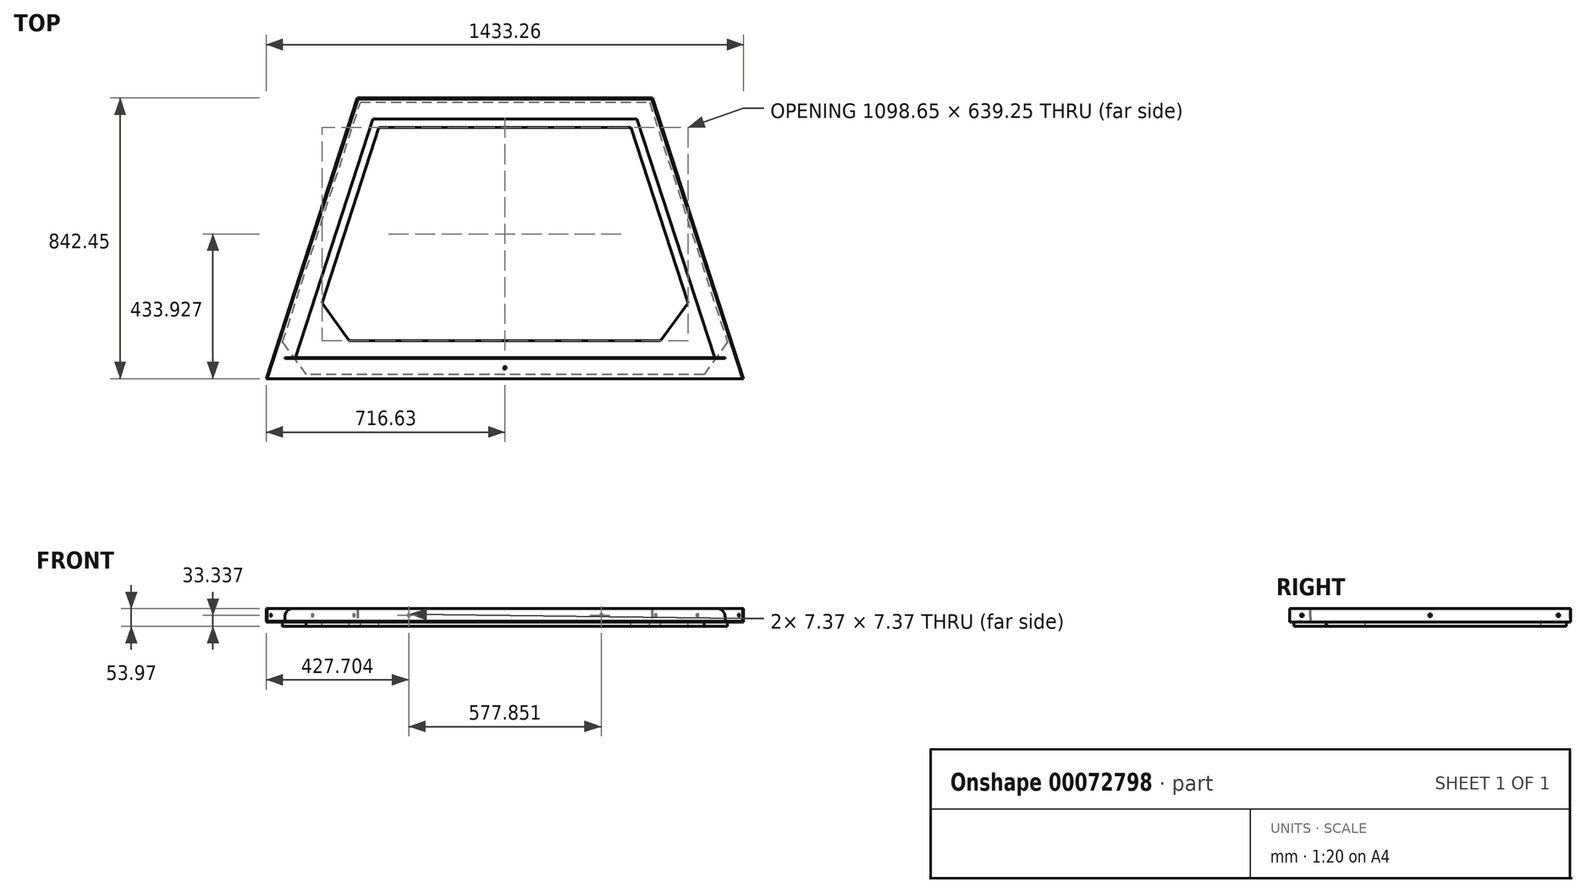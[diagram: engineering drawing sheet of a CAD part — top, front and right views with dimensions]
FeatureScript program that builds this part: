
annotation { "Feature Type Name" : "Feature", "Feature Type Description" : "" }
export const myFeature = defineFeature(function(context is Context, id is Id, definition is map)
    precondition{}
    {
        {
            var Q0;
            Q0=qCreatedBy(makeId("Top.planeOp"),FACE);
            var sketch = newSketch(context, id + "F0", { "sketchPlane" : qUnion([Q0])});
            skCircle(sketch, "E0.cCircle", {"center": v(0, 0) * mm, "radius": 609.6 * mm, "construction": true});
            skLineSegment(sketch, "E0.0", {"start": v(-716.63, -232.85) * mm, "end": v(-442.9, 609.6) * mm});
            skLineSegment(sketch, "E0.1", {"start": v(-442.9, 609.6) * mm, "end": v(442.9, 609.6) * mm});
            skLineSegment(sketch, "E0.2", {"start": v(442.9, 609.6) * mm, "end": v(716.63, -232.85) * mm});
            skPoint(sketch, "E0.0.midPoint", {"position": v(-579.76, 188.38) * mm});
            skLineSegment(sketch, "E1", {"start": v(-716.63, -232.85) * mm, "end": v(716.63, -232.85) * mm});
            skPoint(sketch, "E2.orphan", {"position": v(0, -753.5) * mm});
            skLineSegment(sketch, "E3.0", {"start": v(-629.23, -169.35) * mm, "end": v(-396.76, 546.1) * mm});
            skLineSegment(sketch, "E3.1", {"start": v(-629.23, -169.35) * mm, "end": v(629.23, -169.35) * mm});
            skLineSegment(sketch, "E3.2", {"start": v(396.76, 546.1) * mm, "end": v(629.23, -169.35) * mm});
            skLineSegment(sketch, "E3.3", {"start": v(-396.76, 546.1) * mm, "end": v(396.76, 546.1) * mm});
            skLineSegment(sketch, "E4.0", {"start": v(440.6, 606.43) * mm, "end": v(713.29, -232.85) * mm});
            skLineSegment(sketch, "E4.1", {"start": v(-440.6, 606.43) * mm, "end": v(440.6, 606.43) * mm});
            skLineSegment(sketch, "E4.2", {"start": v(-713.29, -232.85) * mm, "end": v(-440.6, 606.43) * mm});
            skSolve(sketch);
        }
        {
            var Q0;
            Q0=makeQuery(id+"F0.imprint","IMPRINT",FACE,{"disambiguationData":[TD([[makeQuery(id+"F0.imprint","IMPRINT",EDGE,{"derivedFrom":sQuery(id+"F0.wireOp",EDGE,"E0.0")}),-1.0]])]});
            var Q1;
            Q1=makeQuery(id+"F0.imprint","IMPRINT",FACE,{"disambiguationData":[TD([[makeQuery(id+"F0.imprint","IMPRINT",EDGE,{"derivedFrom":sQuery(id+"F0.wireOp",EDGE,"E3.0")}),1.0]])]});
            extrude(context, id + "F1", {"entities" : qUnion([Q0, Q1]), "depth" : 3.17 * mm});
        }
        {
            var Q0;
            Q0=makeQuery(id+"F1.opExtrude","CAP_FACE",FACE,{"disambiguationData":[OSD([sQuery(id+"F0.wireOp",EDGE,"E0.0"),sQuery(id+"F0.wireOp",EDGE,"E0.1"),sQuery(id+"F0.wireOp",EDGE,"E0.2"),sQuery(id+"F0.wireOp",EDGE,"E1"),sQuery(id+"F0.wireOp",EDGE,"E3.0"),sQuery(id+"F0.wireOp",EDGE,"E3.1"),sQuery(id+"F0.wireOp",EDGE,"E3.2"),sQuery(id+"F0.wireOp",EDGE,"E3.3")])],"isStart":false});
            var sketch = newSketch(context, id + "F2", { "sketchPlane" : qUnion([Q0])});
            skLineSegment(sketch, "E5.0", {"start": v(-716.63, -232.85) * mm, "end": v(-442.9, 609.6) * mm});
            skLineSegment(sketch, "E6.0", {"start": v(-442.9, 609.6) * mm, "end": v(442.9, 609.6) * mm});
            skLineSegment(sketch, "E7.0", {"start": v(442.9, 609.6) * mm, "end": v(716.63, -232.85) * mm});
            skLineSegment(sketch, "E8.0", {"start": v(440.6, 606.42) * mm, "end": v(713.29, -232.85) * mm});
            skLineSegment(sketch, "E9.0", {"start": v(-440.6, 606.43) * mm, "end": v(440.6, 606.43) * mm});
            skLineSegment(sketch, "E10.0", {"start": v(-713.29, -232.85) * mm, "end": v(-440.6, 606.43) * mm});
            skLineSegment(sketch, "E11", {"start": v(-716.63, -232.85) * mm, "end": v(-713.29, -232.85) * mm});
            skLineSegment(sketch, "E12", {"start": v(716.63, -232.85) * mm, "end": v(713.29, -232.85) * mm});
            skSolve(sketch);
        }
        {
            var Q0;
            Q0=makeQuery(id+"F2.imprint","IMPRINT",FACE,{"disambiguationData":[TD([[makeQuery(id+"F2.imprint","IMPRINT",EDGE,{"derivedFrom":sQuery(id+"F2.wireOp",EDGE,"E5.0")}),-1.0]])]});
            extrude(context, id + "F3", {"entities" : qUnion([Q0]), "operationType" : NewBodyOperationType.ADD, "depth" : 38.1 * mm});
        }
        {
            var Q0;
            Q0=makeQuery(id+"F1.opExtrude","CAP_FACE",FACE,{"disambiguationData":[OSD([sQuery(id+"F0.wireOp",EDGE,"E0.0"),sQuery(id+"F0.wireOp",EDGE,"E0.1"),sQuery(id+"F0.wireOp",EDGE,"E0.2"),sQuery(id+"F0.wireOp",EDGE,"E1"),sQuery(id+"F0.wireOp",EDGE,"E3.0"),sQuery(id+"F0.wireOp",EDGE,"E3.1"),sQuery(id+"F0.wireOp",EDGE,"E3.2"),sQuery(id+"F0.wireOp",EDGE,"E3.3")])],"isStart":false});
            var sketch = newSketch(context, id + "F4", { "sketchPlane" : qUnion([Q0])});
            skLineSegment(sketch, "E13.0", {"start": v(-629.23, -169.35) * mm, "end": v(629.23, -169.35) * mm});
            skLineSegment(sketch, "E14.0", {"start": v(-660.98, -172.43) * mm, "end": v(660.98, -172.43) * mm});
            skLineSegment(sketch, "E15", {"start": v(-629.23, -169.35) * mm, "end": v(-660.98, -169.35) * mm});
            skLineSegment(sketch, "E16", {"start": v(-660.98, -169.35) * mm, "end": v(-660.98, -172.43) * mm});
            skLineSegment(sketch, "E17", {"start": v(629.23, -169.35) * mm, "end": v(660.98, -169.35) * mm});
            skLineSegment(sketch, "E18", {"start": v(660.98, -169.35) * mm, "end": v(660.98, -172.43) * mm});
            skSolve(sketch);
        }
        {
            var Q0;
            Q0=makeQuery(id+"F4.imprint","IMPRINT",FACE,{"disambiguationData":[TD([[makeQuery(id+"F4.imprint","IMPRINT",EDGE,{"derivedFrom":sQuery(id+"F4.wireOp",EDGE,"E13.0")}),-1.0]])]});
            extrude(context, id + "F5", {"entities" : qUnion([Q0]), "operationType" : NewBodyOperationType.ADD, "depth" : 38.1 * mm});
        }
        {
            var Q0;
            Q0=makeQuery(id+"F5.opExtrude","CAP_EDGE",EDGE,{"disambiguationData":[OSD([sQuery(id+"F4.wireOp",EDGE,"E18")])],"isStart":false});
            var Q1;
            Q1=makeQuery(id+"F5.opExtrude","CAP_EDGE",EDGE,{"disambiguationData":[OSD([sQuery(id+"F4.wireOp",EDGE,"E16")])],"isStart":false});
            fillet(context, id + "F6", {"entities" : qUnion([Q0, Q1]), "radius" : 25.4 * mm, "tangentPropagation" : true, "allowEdgeOverflow" : false});
        }
        {
            var Q0;
            Q0=makeQuery(id+"F3.boolean.opBoolean","MERGE",FACE,{"derivedFrom":[makeQuery(id+"F1.opExtrude","SWEPT_FACE",FACE,{"disambiguationData":[OSD([sQuery(id+"F0.wireOp",EDGE,"E0.2")])]}),makeQuery(id+"F3.opExtrude","SWEPT_FACE",FACE,{"disambiguationData":[OSD([sQuery(id+"F2.wireOp",EDGE,"E7.0")])]})]});
            var sketch = newSketch(context, id + "F7", { "sketchPlane" : qUnion([Q0])});
            skLineSegment(sketch, "E19", {"start": v(442.9, 20.64) * mm, "end": v(404.8, 20.64) * mm, "construction": true});
            skLineSegment(sketch, "E20.rect.bottom", {"start": v(401.12, 16.95) * mm, "end": v(408.48, 16.95) * mm});
            skLineSegment(sketch, "E20.rect.top", {"start": v(401.12, 24.32) * mm, "end": v(408.48, 24.32) * mm});
            skLineSegment(sketch, "E20.rect.left", {"start": v(401.12, 16.95) * mm, "end": v(401.12, 24.32) * mm});
            skLineSegment(sketch, "E20.rect.right", {"start": v(408.48, 16.95) * mm, "end": v(408.48, 24.32) * mm});
            skPoint(sketch, "E20.rect.middle", {"position": v(404.8, 20.64) * mm});
            skLineSegment(sketch, "E21", {"start": v(404.8, 20.64) * mm, "end": v(0, 20.64) * mm, "construction": true});
            skLineSegment(sketch, "E22.rect.bottom", {"start": v(-3.68, 16.95) * mm, "end": v(3.68, 16.95) * mm});
            skLineSegment(sketch, "E22.rect.top", {"start": v(-3.68, 24.32) * mm, "end": v(3.68, 24.32) * mm});
            skLineSegment(sketch, "E22.rect.left", {"start": v(-3.68, 16.95) * mm, "end": v(-3.68, 24.32) * mm});
            skLineSegment(sketch, "E22.rect.right", {"start": v(3.68, 16.95) * mm, "end": v(3.68, 24.32) * mm});
            skPoint(sketch, "E22.rect.middle", {"position": v(0, 20.64) * mm});
            skLineSegment(sketch, "E23", {"start": v(0, 20.64) * mm, "end": v(-404.8, 20.64) * mm, "construction": true});
            skLineSegment(sketch, "E24.rect.bottom", {"start": v(-408.48, 16.95) * mm, "end": v(-401.12, 16.95) * mm});
            skLineSegment(sketch, "E24.rect.top", {"start": v(-408.48, 24.32) * mm, "end": v(-401.12, 24.32) * mm});
            skLineSegment(sketch, "E24.rect.left", {"start": v(-408.48, 16.95) * mm, "end": v(-408.48, 24.32) * mm});
            skLineSegment(sketch, "E24.rect.right", {"start": v(-401.12, 16.95) * mm, "end": v(-401.12, 24.32) * mm});
            skPoint(sketch, "E24.rect.middle", {"position": v(-404.8, 20.64) * mm});
            skLineSegment(sketch, "E25", {"start": v(-404.8, 20.64) * mm, "end": v(-442.9, 20.64) * mm, "construction": true});
            skSolve(sketch);
        }
        {
            var Q0;
            Q0=makeQuery(id+"F7.imprint","IMPRINT",FACE,{"disambiguationData":[TD([[makeQuery(id+"F7.imprint","IMPRINT",EDGE,{"derivedFrom":sQuery(id+"F7.wireOp",EDGE,"E20.rect.bottom")}),1.0]])]});
            var Q1;
            Q1=makeQuery(id+"F7.imprint","IMPRINT",FACE,{"disambiguationData":[TD([[makeQuery(id+"F7.imprint","IMPRINT",EDGE,{"derivedFrom":sQuery(id+"F7.wireOp",EDGE,"E22.rect.bottom")}),1.0]])]});
            var Q2;
            Q2=makeQuery(id+"F7.imprint","IMPRINT",FACE,{"disambiguationData":[TD([[makeQuery(id+"F7.imprint","IMPRINT",EDGE,{"derivedFrom":sQuery(id+"F7.wireOp",EDGE,"E24.rect.bottom")}),1.0]])]});
            extrude(context, id + "F8", {"entities" : qUnion([Q0, Q1, Q2]), "operationType" : NewBodyOperationType.REMOVE, "oppositeDirection" : true, "depth" : 25.4 * mm});
        }
        {
            var Q0;
            Q0=makeQuery(id+"F3.boolean.opBoolean","MERGE",FACE,{"derivedFrom":[makeQuery(id+"F1.opExtrude","SWEPT_FACE",FACE,{"disambiguationData":[OSD([sQuery(id+"F0.wireOp",EDGE,"E0.0")])]}),makeQuery(id+"F3.opExtrude","SWEPT_FACE",FACE,{"disambiguationData":[OSD([sQuery(id+"F2.wireOp",EDGE,"E5.0")])]})]});
            var sketch = newSketch(context, id + "F9", { "sketchPlane" : qUnion([Q0])});
            skLineSegment(sketch, "E26", {"start": v(-442.9, 20.64) * mm, "end": v(-404.8, 20.64) * mm, "construction": true});
            skLineSegment(sketch, "E27", {"start": v(-404.8, 20.64) * mm, "end": v(0, 20.64) * mm, "construction": true});
            skLineSegment(sketch, "E28", {"start": v(0, 20.64) * mm, "end": v(404.8, 20.64) * mm, "construction": true});
            skLineSegment(sketch, "E29", {"start": v(404.8, 20.64) * mm, "end": v(442.9, 20.64) * mm, "construction": true});
            skLineSegment(sketch, "E30.rect.bottom", {"start": v(-401.12, 24.32) * mm, "end": v(-408.48, 24.32) * mm});
            skLineSegment(sketch, "E30.rect.top", {"start": v(-401.12, 16.95) * mm, "end": v(-408.48, 16.95) * mm});
            skLineSegment(sketch, "E30.rect.left", {"start": v(-401.12, 24.32) * mm, "end": v(-401.12, 16.95) * mm});
            skLineSegment(sketch, "E30.rect.right", {"start": v(-408.48, 24.32) * mm, "end": v(-408.48, 16.95) * mm});
            skPoint(sketch, "E30.rect.middle", {"position": v(-404.8, 20.64) * mm});
            skLineSegment(sketch, "E31.rect.bottom", {"start": v(3.68, 24.32) * mm, "end": v(-3.68, 24.32) * mm});
            skLineSegment(sketch, "E31.rect.top", {"start": v(3.68, 16.95) * mm, "end": v(-3.68, 16.95) * mm});
            skLineSegment(sketch, "E31.rect.left", {"start": v(3.68, 24.32) * mm, "end": v(3.68, 16.95) * mm});
            skLineSegment(sketch, "E31.rect.right", {"start": v(-3.68, 24.32) * mm, "end": v(-3.68, 16.95) * mm});
            skPoint(sketch, "E31.rect.middle", {"position": v(0, 20.64) * mm});
            skLineSegment(sketch, "E32.rect.bottom", {"start": v(408.48, 24.32) * mm, "end": v(401.12, 24.32) * mm});
            skLineSegment(sketch, "E32.rect.top", {"start": v(408.48, 16.95) * mm, "end": v(401.12, 16.95) * mm});
            skLineSegment(sketch, "E32.rect.left", {"start": v(408.48, 24.32) * mm, "end": v(408.48, 16.95) * mm});
            skLineSegment(sketch, "E32.rect.right", {"start": v(401.12, 24.32) * mm, "end": v(401.12, 16.95) * mm});
            skPoint(sketch, "E32.rect.middle", {"position": v(404.8, 20.64) * mm});
            skSolve(sketch);
        }
        {
            var Q0;
            Q0=makeQuery(id+"F9.imprint","IMPRINT",FACE,{"disambiguationData":[TD([[makeQuery(id+"F9.imprint","IMPRINT",EDGE,{"derivedFrom":sQuery(id+"F9.wireOp",EDGE,"E30.rect.bottom")}),1.0]])]});
            var Q1;
            Q1=makeQuery(id+"F9.imprint","IMPRINT",FACE,{"disambiguationData":[TD([[makeQuery(id+"F9.imprint","IMPRINT",EDGE,{"derivedFrom":sQuery(id+"F9.wireOp",EDGE,"E31.rect.bottom")}),1.0]])]});
            var Q2;
            Q2=makeQuery(id+"F9.imprint","IMPRINT",FACE,{"disambiguationData":[TD([[makeQuery(id+"F9.imprint","IMPRINT",EDGE,{"derivedFrom":sQuery(id+"F9.wireOp",EDGE,"E32.rect.bottom")}),1.0]])]});
            extrude(context, id + "F10", {"entities" : qUnion([Q0, Q1, Q2]), "operationType" : NewBodyOperationType.REMOVE, "oppositeDirection" : true, "depth" : 25.4 * mm});
        }
        {
            var Q0;
            Q0=makeQuery(id+"F1.opExtrude","CAP_FACE",FACE,{"disambiguationData":[OSD([sQuery(id+"F0.wireOp",EDGE,"E0.0"),sQuery(id+"F0.wireOp",EDGE,"E0.1"),sQuery(id+"F0.wireOp",EDGE,"E0.2"),sQuery(id+"F0.wireOp",EDGE,"E1"),sQuery(id+"F0.wireOp",EDGE,"E3.0"),sQuery(id+"F0.wireOp",EDGE,"E3.1"),sQuery(id+"F0.wireOp",EDGE,"E3.2"),sQuery(id+"F0.wireOp",EDGE,"E3.3")])],"isStart":true});
            var sketch = newSketch(context, id + "F11", { "sketchPlane" : qUnion([Q0])});
            skLineSegment(sketch, "E33.0", {"start": v(-667.75, 123.52) * mm, "end": v(-433.67, -596.9) * mm});
            skLineSegment(sketch, "E33.1", {"start": v(597.55, 220.15) * mm, "end": v(-597.55, 220.15) * mm});
            skLineSegment(sketch, "E33.2", {"start": v(433.67, -596.9) * mm, "end": v(667.75, 123.52) * mm});
            skLineSegment(sketch, "E33.3", {"start": v(-433.67, -596.9) * mm, "end": v(433.67, -596.9) * mm});
            skLineSegment(sketch, "E34.0", {"start": v(-378.31, -520.7) * mm, "end": v(378.31, -520.7) * mm});
            skLineSegment(sketch, "E34.1", {"start": v(-549.33, 5.63) * mm, "end": v(-378.31, -520.7) * mm});
            skLineSegment(sketch, "E34.3", {"start": v(378.31, -520.7) * mm, "end": v(549.33, 5.63) * mm});
            skLineSegment(sketch, "E35.0", {"start": v(467.29, 118.55) * mm, "end": v(-467.29, 118.55) * mm});
            skLineSegment(sketch, "E36", {"start": v(549.33, 5.63) * mm, "end": v(467.29, 118.55) * mm});
            skLineSegment(sketch, "E37", {"start": v(-549.33, 5.63) * mm, "end": v(-467.29, 118.55) * mm});
            skLineSegment(sketch, "E38", {"start": v(-667.75, 123.52) * mm, "end": v(-597.55, 220.15) * mm});
            skLineSegment(sketch, "E39", {"start": v(667.75, 123.52) * mm, "end": v(597.55, 220.15) * mm});
            skPoint(sketch, "E40.orphan", {"position": v(699.15, 220.15) * mm});
            skPoint(sketch, "E41.orphan", {"position": v(-699.15, 220.15) * mm});
            skSolve(sketch);
        }
        {
            var Q0;
            Q0=makeQuery(id+"F11.imprint","IMPRINT",FACE,{"disambiguationData":[TD([[makeQuery(id+"F11.imprint","IMPRINT",EDGE,{"derivedFrom":sQuery(id+"F11.wireOp",EDGE,"E34.0")}),-1.0]])]});
            var Q1;
            Q1=makeQuery(id+"F11.imprint","IMPRINT",FACE,{"disambiguationData":[TD([[makeQuery(id+"F11.imprint","IMPRINT",EDGE,{"derivedFrom":sQuery(id+"F11.wireOp",EDGE,"E33.0")}),1.0]])]});
            extrude(context, id + "F12", {"entities" : qUnion([Q0, Q1]), "depth" : 12.7 * mm});
        }
        {
            var Q0;
            Q0=makeQuery(id+"F3.boolean.opBoolean","MERGE",FACE,{"derivedFrom":[makeQuery(id+"F1.opExtrude","SWEPT_FACE",FACE,{"disambiguationData":[OSD([sQuery(id+"F0.wireOp",EDGE,"E0.1")])]}),makeQuery(id+"F3.opExtrude","SWEPT_FACE",FACE,{"disambiguationData":[OSD([sQuery(id+"F2.wireOp",EDGE,"E6.0")])]})]});
            var sketch = newSketch(context, id + "F13", { "sketchPlane" : qUnion([Q0])});
            skLineSegment(sketch, "E42", {"start": v(442.9, 20.64) * mm, "end": v(288.93, 20.64) * mm, "construction": true});
            skPoint(sketch, "E42.startSnap0", {"position": v(442.9, 20.64) * mm});
            skLineSegment(sketch, "E43", {"start": v(288.93, 20.64) * mm, "end": v(-288.93, 20.64) * mm, "construction": true});
            skLineSegment(sketch, "E44", {"start": v(-288.93, 20.64) * mm, "end": v(-442.9, 20.64) * mm, "construction": true});
            skLineSegment(sketch, "E45.rect.bottom", {"start": v(285.24, 24.32) * mm, "end": v(292.6, 24.32) * mm});
            skLineSegment(sketch, "E45.rect.top", {"start": v(285.24, 16.95) * mm, "end": v(292.6, 16.95) * mm});
            skLineSegment(sketch, "E45.rect.left", {"start": v(285.24, 24.32) * mm, "end": v(285.24, 16.95) * mm});
            skLineSegment(sketch, "E45.rect.right", {"start": v(292.6, 24.32) * mm, "end": v(292.6, 16.95) * mm});
            skPoint(sketch, "E45.rect.middle", {"position": v(288.93, 20.64) * mm});
            skLineSegment(sketch, "E46.rect.bottom", {"start": v(-292.6, 24.32) * mm, "end": v(-285.24, 24.32) * mm});
            skLineSegment(sketch, "E46.rect.top", {"start": v(-292.6, 16.95) * mm, "end": v(-285.24, 16.95) * mm});
            skLineSegment(sketch, "E46.rect.left", {"start": v(-292.6, 24.32) * mm, "end": v(-292.6, 16.95) * mm});
            skLineSegment(sketch, "E46.rect.right", {"start": v(-285.24, 24.32) * mm, "end": v(-285.24, 16.95) * mm});
            skPoint(sketch, "E46.rect.middle", {"position": v(-288.93, 20.64) * mm});
            skSolve(sketch);
        }
        {
            var Q0;
            Q0=makeQuery(id+"F13.imprint","IMPRINT",FACE,{"disambiguationData":[TD([[makeQuery(id+"F13.imprint","IMPRINT",EDGE,{"derivedFrom":sQuery(id+"F13.wireOp",EDGE,"E45.rect.bottom")}),-1.0]])]});
            var Q1;
            Q1=makeQuery(id+"F13.imprint","IMPRINT",FACE,{"disambiguationData":[TD([[makeQuery(id+"F13.imprint","IMPRINT",EDGE,{"derivedFrom":sQuery(id+"F13.wireOp",EDGE,"E46.rect.bottom")}),-1.0]])]});
            extrude(context, id + "F14", {"entities" : qUnion([Q0, Q1]), "operationType" : NewBodyOperationType.REMOVE, "oppositeDirection" : true, "depth" : 25.4 * mm});
        }
        {
            var Q0;
            Q0=makeQuery(id+"F1.opExtrude","CAP_FACE",FACE,{"disambiguationData":[OSD([sQuery(id+"F0.wireOp",EDGE,"E0.0"),sQuery(id+"F0.wireOp",EDGE,"E0.1"),sQuery(id+"F0.wireOp",EDGE,"E0.2"),sQuery(id+"F0.wireOp",EDGE,"E1"),sQuery(id+"F0.wireOp",EDGE,"E3.0"),sQuery(id+"F0.wireOp",EDGE,"E3.1"),sQuery(id+"F0.wireOp",EDGE,"E3.2"),sQuery(id+"F0.wireOp",EDGE,"E3.3")])],"isStart":true});
            var sketch = newSketch(context, id + "F15", { "sketchPlane" : qUnion([Q0])});
            skLineSegment(sketch, "E47", {"start": v(0, 169.35) * mm, "end": v(0, 232.85) * mm, "construction": true});
            skPoint(sketch, "E48", {"position": v(0, 201.1) * mm});
            skSolve(sketch);
        }
        {
            var Q0;
            Q0=sQuery(id+"F15.wireOp",VERTEX,"E48");
            var Q1;
            Q1=makeQuery(id+"F1.opExtrude","SWEPT_BODY",BODY,{"disambiguationData":[OSD([sQuery(id+"F0.wireOp",EDGE,"E0.0"),sQuery(id+"F0.wireOp",EDGE,"E0.1"),sQuery(id+"F0.wireOp",EDGE,"E0.2"),sQuery(id+"F0.wireOp",EDGE,"E1"),sQuery(id+"F0.wireOp",EDGE,"E3.0"),sQuery(id+"F0.wireOp",EDGE,"E3.1"),sQuery(id+"F0.wireOp",EDGE,"E3.2"),sQuery(id+"F0.wireOp",EDGE,"E3.3")])]});
            hole(context, id + "F16", {"style" : HoleStyle.C_SINK, "holeDiameter" : 6.35 * mm, "cSinkDiameter" : 12.7 * mm, "endStyle" : HoleEndStyle.THROUGH, "locations" : qUnion([Q0]), "scope" : qUnion([Q1]), "cSinkAngle" : 90 * degree});
        }
    });
